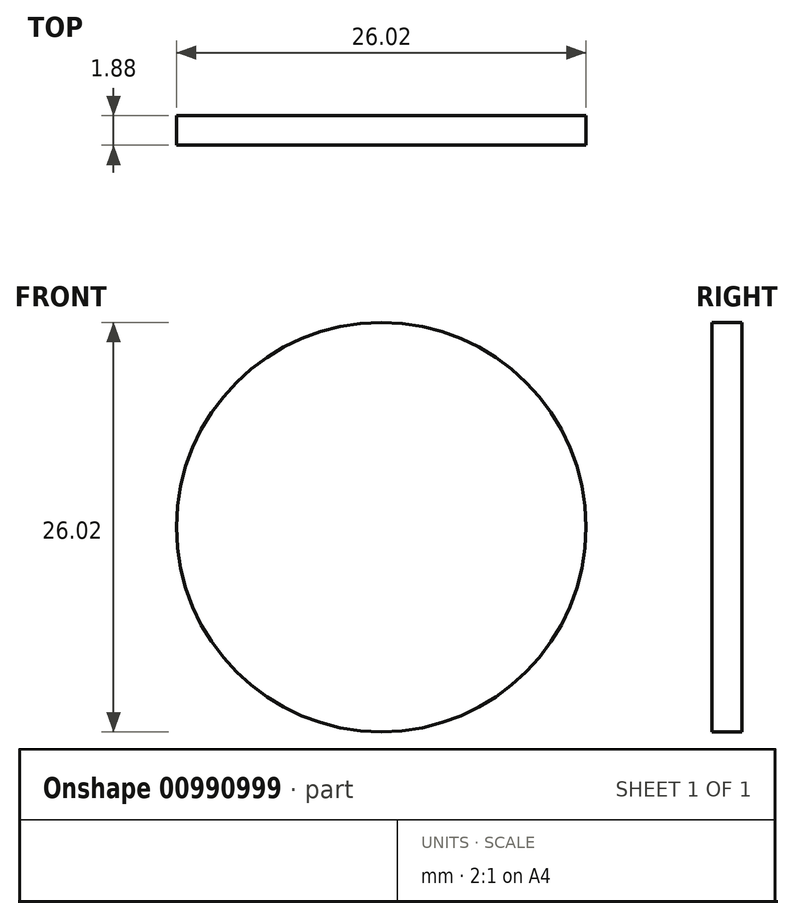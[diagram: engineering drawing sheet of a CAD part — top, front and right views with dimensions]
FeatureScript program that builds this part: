
annotation { "Feature Type Name" : "Feature", "Feature Type Description" : "" }
export const myFeature = defineFeature(function(context is Context, id is Id, definition is map)
    precondition{}
    {
        {
            var Q0;
            Q0=qCreatedBy(makeId("Front.planeOp"),FACE);
            var sketch = newSketch(context, id + "F0", { "sketchPlane" : qUnion([Q0])});
            skCircle(sketch, "E0", {"center": v(0, 0) * mm, "radius": 13 * mm});
            skSolve(sketch);
        }
        {
            var Q0;
            Q0 = qSketchRegion(id + "F0", true);
            extrude(context, id + "F1", {"entities" : qUnion([Q0]), "depth" : 1.88 * mm, "offsetDistance" : 25 * mm});
        }
    });
